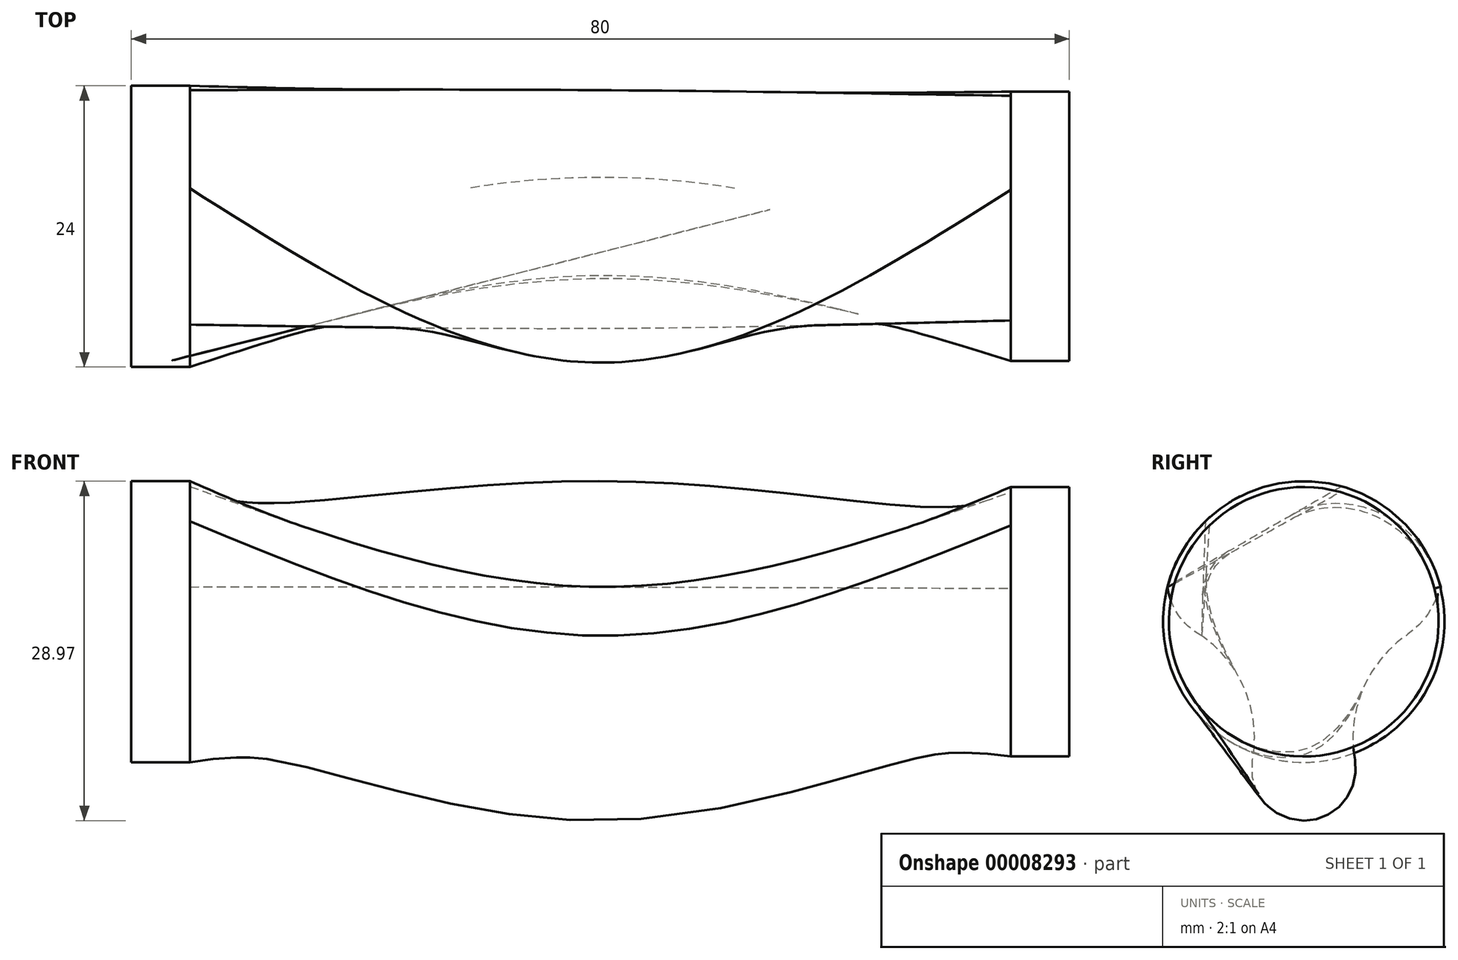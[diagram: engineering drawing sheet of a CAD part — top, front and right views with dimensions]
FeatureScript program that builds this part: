
annotation { "Feature Type Name" : "Feature", "Feature Type Description" : "" }
export const myFeature = defineFeature(function(context is Context, id is Id, definition is map)
    precondition{}
    {
        {
            var Q0;
            Q0=qCreatedBy(makeId("Right.planeOp"),FACE);
            cPlane(context, id + "F0", {"entities" : qUnion([Q0]), "cplaneType" : CPlaneType.OFFSET, "offset" : 35 * mm, "width" : 150 * mm, "height" : 150 * mm});
        }
        {
            var Q0;
            Q0=qCreatedBy(id+"F0.planeOp",FACE);
            cPlane(context, id + "F1", {"entities" : qUnion([Q0]), "cplaneType" : CPlaneType.OFFSET, "offset" : 35 * mm, "width" : 150 * mm, "height" : 150 * mm});
        }
        {
            var Q0;
            Q0=qCreatedBy(makeId("Right.planeOp"),FACE);
            var sketch = newSketch(context, id + "F2", { "sketchPlane" : qUnion([Q0])});
            skCircle(sketch, "E0", {"center": v(0, 0) * mm, "radius": 12 * mm});
            skLineSegment(sketch, "E1", {"start": v(0, 0) * mm, "end": v(0, 12) * mm});
            skSolve(sketch);
        }
        {
            var Q0;
            Q0=qCreatedBy(makeId("Right.planeOp"),FACE);
            var sketch = newSketch(context, id + "F3", { "sketchPlane" : qUnion([Q0])});
            skLineSegment(sketch, "E2", {"start": v(0, 0) * mm, "end": v(0, 12.15) * mm});
            skSolve(sketch);
        }
        {
            var Q0;
            Q0=qCreatedBy(id+"F0.planeOp",FACE);
            var sketch = newSketch(context, id + "F4", { "sketchPlane" : qUnion([Q0])});
            skLineSegment(sketch, "E3", {"start": v(-7.03, 0) * mm, "end": v(7.43, 0) * mm});
            skLineSegment(sketch, "E4", {"start": v(0, -6.37) * mm, "end": v(0, 0) * mm});
            skPoint(sketch, "E5.trimOffspring.end.orphan", {"position": v(12.5, 0) * mm});
            skLineSegment(sketch, "E6", {"start": v(0, 0) * mm, "end": v(0, 12) * mm});
            skPoint(sketch, "E7.start.orphan", {"position": v(-12.5, 0) * mm});
            skArc(sketch, "E8.0", {"start": v(11.63, 2.97) * mm, "mid": v(0, 12) * mm, "end": v(-11.63, 2.97) * mm});
            skArc(sketch, "E9.0", {"start": v(-4.34, -11.6) * mm, "mid": v(-5.03, -5.78) * mm, "end": v(-8.7, -1.2) * mm});
            skArc(sketch, "E10.0", {"start": v(4.34, -11.6) * mm, "mid": v(5.03, -5.78) * mm, "end": v(8.7, -1.2) * mm});
            skArc(sketch, "E11", {"start": v(-4.34, -11.6) * mm, "mid": v(0, -16.97) * mm, "end": v(4.34, -11.6) * mm});
            skArc(sketch, "E12", {"start": v(-11.63, 2.97) * mm, "mid": v(-10.66, 0.54) * mm, "end": v(-8.7, -1.2) * mm});
            skArc(sketch, "E13", {"start": v(8.7, -1.2) * mm, "mid": v(10.56, 0.6) * mm, "end": v(11.63, 2.97) * mm});
            skPoint(sketch, "E14.0.MirrorCS.start.orphan", {"position": v(12.11, 3.1) * mm});
            skPoint(sketch, "E15.0.MirrorCS.end.orphan", {"position": v(9, -1.6) * mm});
            skPoint(sketch, "E16.end.orphan", {"position": v(4.83, -11.53) * mm});
            skPoint(sketch, "E17.start.orphan", {"position": v(-4.83, -11.53) * mm});
            skPoint(sketch, "E18.end.orphan", {"position": v(-9, -1.6) * mm});
            skPoint(sketch, "E18.start.orphan", {"position": v(-12.11, 3.1) * mm});
            skSolve(sketch);
        }
        {
            var Q0;
            Q0=qCreatedBy(id+"F1.planeOp",FACE);
            var sketch = newSketch(context, id + "F5", { "sketchPlane" : qUnion([Q0])});
            skCircle(sketch, "E19", {"center": v(0, 0) * mm, "radius": 11.5 * mm});
            skSolve(sketch);
        }
        {
            var Q0;
            Q0=makeQuery(id+"F2.imprint","IMPRINT",FACE,{"disambiguationData":[TD([[makeQuery(id+"F2.imprint","IMPRINT",EDGE,{"derivedFrom":sQuery(id+"F2.wireOp",EDGE,"E0")}),1.0]])]});
            var Q1;
            Q1=makeQuery(id+"F4.imprint","IMPRINT",FACE,{"disambiguationData":[TD([[makeQuery(id+"F4.imprint","IMPRINT",EDGE,{"derivedFrom":sQuery(id+"F4.wireOp",EDGE,"E9.0")}),-1.0]])]});
            var Q2;
            Q2=makeQuery(id+"F5.imprint","IMPRINT",FACE,{"disambiguationData":[TD([[makeQuery(id+"F5.imprint","IMPRINT",EDGE,{"derivedFrom":sQuery(id+"F5.wireOp",EDGE,"E19")}),1.0]])]});
            var Q3;
            Q3=sQuery(id+"F3.wireOp",VERTEX,"E2.end");
            var Q4;
            Q4=sQuery(id+"F4.wireOp",VERTEX,"E6.end");
            loft(context, id + "F6", {"sheetProfilesArray" : [{ "sheetProfileEntities" : qUnion([Q0]) }, { "sheetProfileEntities" : qUnion([Q1]) }, { "sheetProfileEntities" : qUnion([Q2]) }], "connections" : [{ "connectionEntities" : qUnion([Q3, Q4]), "connectionEdgeQueries" : qUnion([]), "connectionEdgeParameters" : [] }]});
        }
        {
            var Q0;
            Q0=makeQuery(id+"F6.opLoft","CAP_FACE",FACE,{"disambiguationData":[OSD([makeQuery(id+"F5.imprint","IMPRINT",FACE,{"disambiguationData":[TD([[makeQuery(id+"F5.imprint","IMPRINT",EDGE,{"derivedFrom":sQuery(id+"F5.wireOp",EDGE,"E19")}),1.0]])]})])],"isStart":true});
            extrude(context, id + "F7", {"entities" : qUnion([Q0]), "operationType" : NewBodyOperationType.ADD, "depth" : 5 * mm});
        }
        {
            var Q0;
            Q0=makeQuery(id+"F6.opLoft","CAP_FACE",FACE,{"disambiguationData":[OSD([makeQuery(id+"F2.imprint","IMPRINT",FACE,{"disambiguationData":[TD([[makeQuery(id+"F2.imprint","IMPRINT",EDGE,{"derivedFrom":sQuery(id+"F2.wireOp",EDGE,"E0")}),1.0]])]})])],"isStart":true});
            extrude(context, id + "F8", {"entities" : qUnion([Q0]), "operationType" : NewBodyOperationType.ADD, "depth" : 5 * mm});
        }
    });
